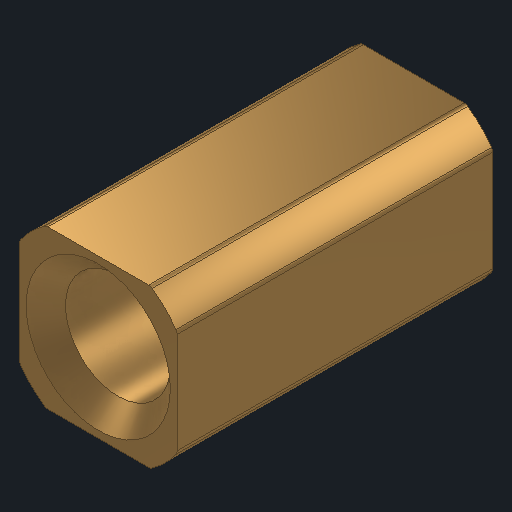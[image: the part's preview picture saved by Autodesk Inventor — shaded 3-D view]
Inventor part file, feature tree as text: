
AUTODESK INVENTOR PART (.ipt)
format: ipt  version: 2024 (Build 280153000, 153)  size: 163,840 bytes
history: native  units: in
note: dims shown in document units (in); Inventor stores cm internally (conversion verified against a paired STEP export)
features: other x3, sketch x2
ambient origin geometry x8: Origin, YZ Plane, XZ Plane, XY Plane, X Axis, Y Axis, Z Axis, Center Point
bodies: Solid1 (feature_tree)
feature tree (5):
  other  "HS Shaft Adapter Circle.ipt"
  other  "Solid1::HS Shaft Adapter Circle.ipt"
  other  "TaggingFeature1"
  sketch  "Sketch1"  dims[d0=0.3937in]
  sketch  "Sketch2"
